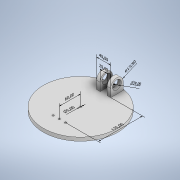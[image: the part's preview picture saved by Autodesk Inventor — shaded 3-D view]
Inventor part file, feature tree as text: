
AUTODESK INVENTOR PART (.ipt)
format: ipt  version: 2021 (Build 250183000, 183)  size: 288,768 bytes
history: native  units: mm
features: extrude x15, sketch x15, other x8, thicken_offset x2
ambient origin geometry x8: Origin, YZ Plane, XZ Plane, XY Plane, X Axis, Y Axis, Z Axis, Center Point
bodies: Solid1 (feature_tree)
feature tree (40):
  other  "Annotations"
  extrude  "Extrusion1"  Depth=10.0mm TaperAngle=0.0deg
  extrude  "Extrusion2"  Depth=20.0mm
  extrude  "Extrusion3"  Depth=17.5mm
  extrude  "Extrusion4"  Depth=5.0mm
  extrude  "Extrusion5"  Depth=10.0mm TaperAngle=0.0deg
  extrude  "Extrusion6"  Depth=10.0mm TaperAngle=0.0deg
  extrude  "Extrusion7"  Depth=15.0mm
  extrude  "Extrusion8"  Depth=30.0mm
  thicken_offset  "Thicken1"
  thicken_offset  "Thicken2"
  extrude  "Extrusion9"  Depth=15.0mm
  sketch  "Sketch11"  dims[d26=30.0mm d27=0.0mm d28=25.0mm]
  extrude  "Extrusion10"  Depth=30.0mm
  extrude  "Extrusion11"  Depth=15.0mm
  extrude  "Extrusion12"  Depth=30.0mm TaperAngle=0.0deg
  extrude  "Extrusion13"  Depth=10.0mm TaperAngle=0.0deg
  extrude  "Extrusion14"  Depth=100.0mm
  extrude  "Extrusion15"  Depth=10.0mm
  sketch  "Sketch1"  dims[d0=210.0mm d1=10.0mm d2=0.0mm]
  sketch  "Sketch2"  dims[d4=80.0mm d5=20.0mm]
  sketch  "Sketch3"  dims[d6=17.5mm d7=17.5mm]
  sketch  "Sketch4"  dims[d8=5.0mm d9=5.0mm]
  sketch  "Sketch5"  dims[d10=5.0mm d11=10.0mm d12=0.0mm]
  sketch  "Sketch6"  dims[d13=5.0mm d14=10.0mm d15=0.0mm]
  sketch  "Sketch7"  dims[d20=15.0mm d21=15.0mm]
  sketch  "Sketch8"  dims[d22=30.0mm d23=30.0mm]
  sketch  "Sketch10"  dims[d24=7.5mm d25=15.0mm]
  sketch  "Sketch12"  dims[d29=15.0mm d30=15.0mm]
  sketch  "Sketch13"  dims[d31=180.0deg d32=30.0mm d33=0.0mm]
  sketch  "Sketch14"  dims[d34=10.0mm d35=15.0mm d36=0.0mm]
  sketch  "Sketch15"  dims[d37=15.0mm d38=0.0mm d42=100.0mm]
  sketch  "Sketch16"  dims[d43=10.0mm d44=10.0mm d45=35.0mm d46=10.0mm d47=10.0mm d48=35.0mm d49=35.0mm d50=0.0mm d56=5.0mm d57=5.0mm d58=5.0mm d59=5.0mm d60=22.5mm d61=25.0mm d62=40.0mm d63=0.0mm d73=35.0mm d74=35.0mm d75=40.0mm d78=35.0mm d79=40.0mm d80=0.0mm d81=40.0mm d82=0.0mm d83=10.0mm d84=20.0mm d85=150.0mm d86=0.0mm d87=150.0mm d88=0.0mm d89=100.0mm d90=20.0mm d91=35.0mm d92=10.0mm d93=20.0mm d94=10.0mm d95=35.0mm d96=10.0mm d97=40.0mm d98=0.0mm d99=17.5mm d100=25.0mm d101=40.0mm d102=0.0mm d103=5.545225mm d104=125.0mm d105=54.333582mm d106=17.5mm d107=45.805267mm d108=25.0mm d109=3.727279mm d110=3.706863mm d111=20.0mm d112=4.477367mm d113=6.339857mm d114=40.0mm d16=46.771507mm d17=5.0mm d18=60.0mm]
  other  "Diameter Dimension 1"
  other  "Linear Dimension 1"
  other  "Linear Dimension 2"
  other  "Radial Dimension 1"
  other  "Diameter Dimension 2"
  other  "Linear Dimension 3"
  other  "Linear Dimension 4"
